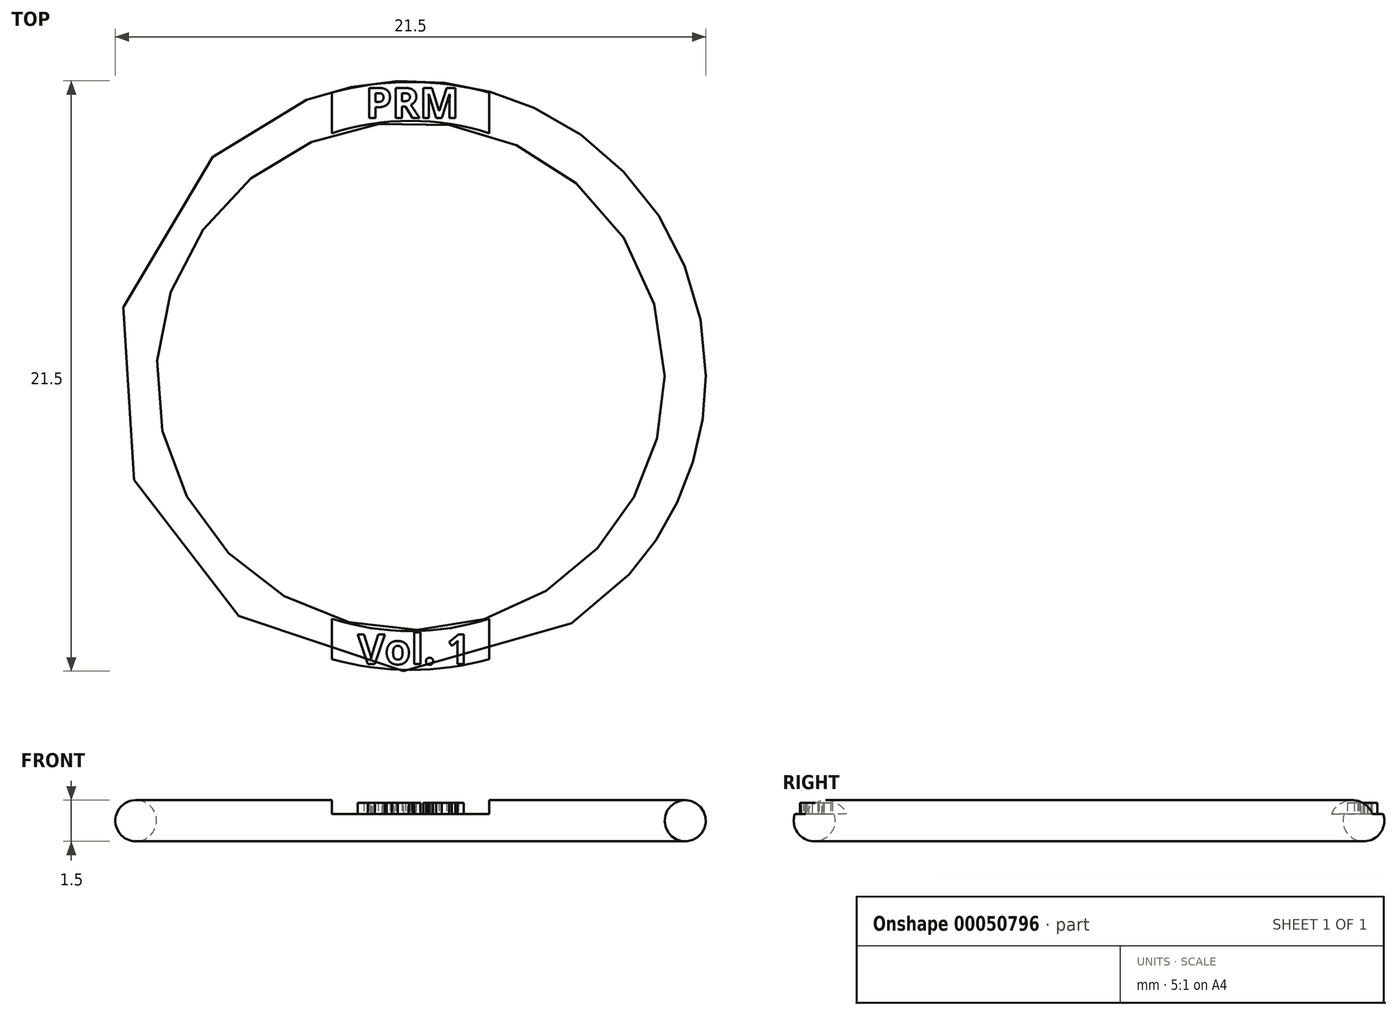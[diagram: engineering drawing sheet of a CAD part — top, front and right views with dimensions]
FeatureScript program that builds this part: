
annotation { "Feature Type Name" : "Feature", "Feature Type Description" : "" }
export const myFeature = defineFeature(function(context is Context, id is Id, definition is map)
    precondition{}
    {
        {
            var Q0;
            Q0=qCreatedBy(makeId("Right.planeOp"),FACE);
            var sketch = newSketch(context, id + "F0", { "sketchPlane" : qUnion([Q0])});
            skLineSegment(sketch, "E0", {"start": v(0, 0) * mm, "end": v(0, 4.24) * mm, "construction": true});
            skCircle(sketch, "E1", {"center": v(-10, 0) * mm, "radius": 0.75 * mm});
            skPoint(sketch, "E2", {"position": v(-10, 0.75) * mm});
            skSolve(sketch);
        }
        {
            var Q0;
            Q0=makeQuery(id+"F0.imprint","IMPRINT",FACE,{"disambiguationData":[TD([[makeQuery(id+"F0.imprint","IMPRINT",EDGE,{"derivedFrom":sQuery(id+"F0.wireOp",EDGE,"E1")}),1.0]])]});
            var Q1;
            Q1=sQuery(id+"F0.wireOp",EDGE,"E0");
            revolve(context, id + "F1", {"entities" : qUnion([Q0]), "axis" : qUnion([Q1]), "revolveType" : RevolveType.FULL});
        }
        {
            var Q0;
            Q0=sQuery(id+"F0.wireOp",VERTEX,"E2");
            var Q1;
            Q1=qCreatedBy(makeId("Top.planeOp"),FACE);
            cPlane(context, id + "F2", {"entities" : qUnion([Q0, Q1]), "cplaneType" : CPlaneType.PLANE_POINT, "offset" : 150 * mm, "width" : 150 * mm, "height" : 150 * mm});
        }
        {
            var Q0;
            Q0=qCreatedBy(id+"F2.planeOp",FACE);
            var sketch = newSketch(context, id + "F3", { "sketchPlane" : qUnion([Q0])});
            skPoint(sketch, "E3.0", {"position": v(0, 0) * mm});
            skLineSegment(sketch, "E4.rect.bottom", {"start": v(-2.87, 15) * mm, "end": v(2.87, 15) * mm});
            skLineSegment(sketch, "E4.rect.top", {"start": v(-2.87, -15) * mm, "end": v(2.87, -15) * mm});
            skLineSegment(sketch, "E4.rect.left", {"start": v(-2.87, 15) * mm, "end": v(-2.87, -15) * mm});
            skLineSegment(sketch, "E4.rect.right", {"start": v(2.87, 15) * mm, "end": v(2.87, -15) * mm});
            skSolve(sketch);
        }
        {
            var Q0;
            Q0=makeQuery(id+"F3.imprint","IMPRINT",FACE,{"disambiguationData":[TD([[makeQuery(id+"F3.imprint","IMPRINT",EDGE,{"derivedFrom":sQuery(id+"F3.wireOp",EDGE,"E4.rect.bottom")}),-1.0]])]});
            extrude(context, id + "F4", {"entities" : qUnion([Q0]), "operationType" : NewBodyOperationType.REMOVE, "oppositeDirection" : true, "depth" : 0.5 * mm});
        }
        {
            var Q0;
            Q0=makeQuery(id+"F4.boolean.opBoolean","COPY",FACE,{"derivedFrom":makeQuery(id+"F4.opExtrude","CAP_FACE",FACE,{"disambiguationData":[OSD([sQuery(id+"F3.wireOp",EDGE,"E4.rect.bottom"),sQuery(id+"F3.wireOp",EDGE,"E4.rect.top"),sQuery(id+"F3.wireOp",EDGE,"E4.rect.left"),sQuery(id+"F3.wireOp",EDGE,"E4.rect.right")])],"isStart":false})});
            var sketch = newSketch(context, id + "F5", { "sketchPlane" : qUnion([Q0])});
            skText(sketch, "E5", { "text": "Vol. 1", "fontName": "OpenSans-Bold.ttf"});
            skText(sketch, "E6", { "text": "PRM", "fontName": "OpenSans-Bold.ttf"});
            const initialGuessF5  = {"E5": [-0.00193, -0.0105, 1, 0, 0.0011], "E6": [-0.00164, 0.0094, 1, 0, 0.0011]};
            skSetInitialGuess(sketch, initialGuessF5);
            skSolve(sketch);
        }
        {
            var Q0;
            Q0=qSketchRegion(id+"F5",true);
            extrude(context, id + "F6", {"entities" : qUnion([Q0]), "operationType" : NewBodyOperationType.ADD, "depth" : 0.4 * mm});
        }
    });
